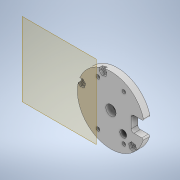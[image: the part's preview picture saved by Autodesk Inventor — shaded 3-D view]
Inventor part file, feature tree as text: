
AUTODESK INVENTOR PART (.ipt)
format: ipt  version: 2022 (Build 260153000, 153)  size: 320,000 bytes
history: native  units: in
note: dims shown in document units (in); Inventor stores cm internally (conversion verified against a paired STEP export)
features: reference x11, extrude x8, sketch x8, other x6, plane x4, chamfer x1
ambient origin geometry x8: Origin, YZ Plane, XZ Plane, XY Plane, X Axis, Y Axis, Z Axis, Center Point
bodies: Solid1 (feature_tree)
feature tree (38):
  plane  "Work Plane1"
  extrude  "Extrusion1"  Depth=0.1969in
  extrude  "Extrusion2"  Depth=1.0in
  plane  "Arbeitsebene4"
  extrude  "Extrusion5"  TaperAngle=0.0deg  [1 undecoded]
  plane  "Arbeitsebene3"
  extrude  "Extrusion6"  Depth=0.1102in
  plane  "Arbeitsebene2"
  extrude  "Extrusion7"  Depth=0.0787in
  extrude  "Extrusion10"  Depth=0.0394in TaperAngle=0.0deg
  extrude  "Extrusion11"  Depth=0.3937in
  chamfer  "Fase3"  Distance=0.2362in
  extrude  "Extrusion12"  Depth=0.2165in
  sketch  "Sketch1"  dims[d0=0.1969in d1=0.0in d2=0.315in]
  reference  "Reference1"
  reference  "Reference2"
  reference  "Reference3"
  reference  "Reference4"
  reference  "Reference5"
  reference  "Reference6"
  reference  "Reference7"
  reference  "Reference8"
  sketch  "Sketch2"  dims[d3=0.311in d4=1.0in d5=-0.0137in]
  sketch  "Sketch7"  dims[d30=0.1102in d31=0.0in d32=0.0in]
  sketch  "Sketch8"  dims[d33=0.1102in d34=0.1102in]
  sketch  "Sketch9"  dims[d35=0.0in d36=0.0in d37=0.0787in]
  sketch  "Skizze12"  dims[d38=0.0004in d39=0.0in d51=0.0394in d52=0.0in]
  sketch  "Skizze13"  dims[d53=0.2638in d54=0.3937in d55=0.2362in d56=0.0in]
  sketch  "Skizze14"  dims[d57=0.0591in d58=0.0787in d59=45.0deg d60=0.2165in d61=0.2165in d62=0.2165in d63=0.0787in d64=0.0in]
  reference  "Referenz27"
  reference  "Referenz28"
  reference  "Referenz29"
  other  "Assembly1"
  other  "Assembly_MANATEE_V0_Manatee_middle2_v0_18:1"
  other  "Matchboxscope_v1.iam"
  other  "DIN 912 - ersetzt durch DIN EN ISO 4762 M3 x 25:2"
  other  "DIN 912 - ersetzt durch DIN EN ISO 4762 M3 x 25:1"
  other  "DIN 912 - ersetzt durch DIN EN ISO 4762 M3 x 25:3"
note: 1 required parameter value undecoded (feature->parameter linkage not recoverable at this tier; creation-order binding heuristic only, values carry confidence <= 0.55)
